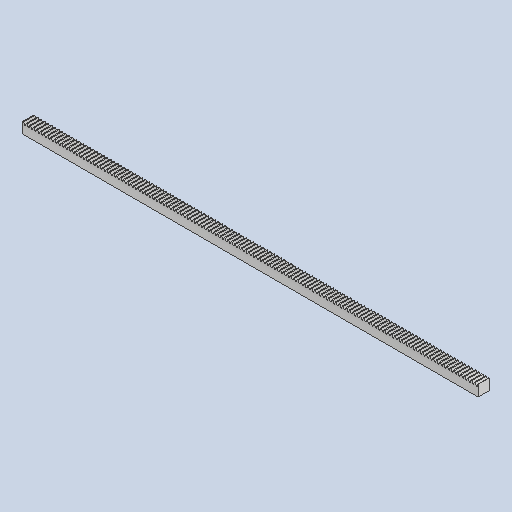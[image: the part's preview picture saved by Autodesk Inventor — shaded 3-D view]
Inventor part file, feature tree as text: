
AUTODESK INVENTOR PART (.ipt)
format: ipt  version: 2023 (Build 270158000, 158)  size: 1,179,648 bytes
history: imported  units: in
note: dims shown in document units (in); Inventor stores cm internally (conversion verified against a paired STEP export)
features: other x3, sketch x1, imported_body x1
ambient origin geometry x8: Origin, YZ Plane, XZ Plane, XY Plane, X Axis, Y Axis, Z Axis, Center Point
bodies: Solid1 (imported_parasolid)
feature tree (5):
  other  "rack2.ipt"
  other  "Solid1::rack2.ipt"
  other  "TaggingFeature1"
  sketch  "Sketch1"  dims[d0=0.3937in]
  imported_body  NMx_Import_Brep_tag  [imported B-rep: ~792 faces, bbox_mm=[411.8, 10.0, 10.0]]
